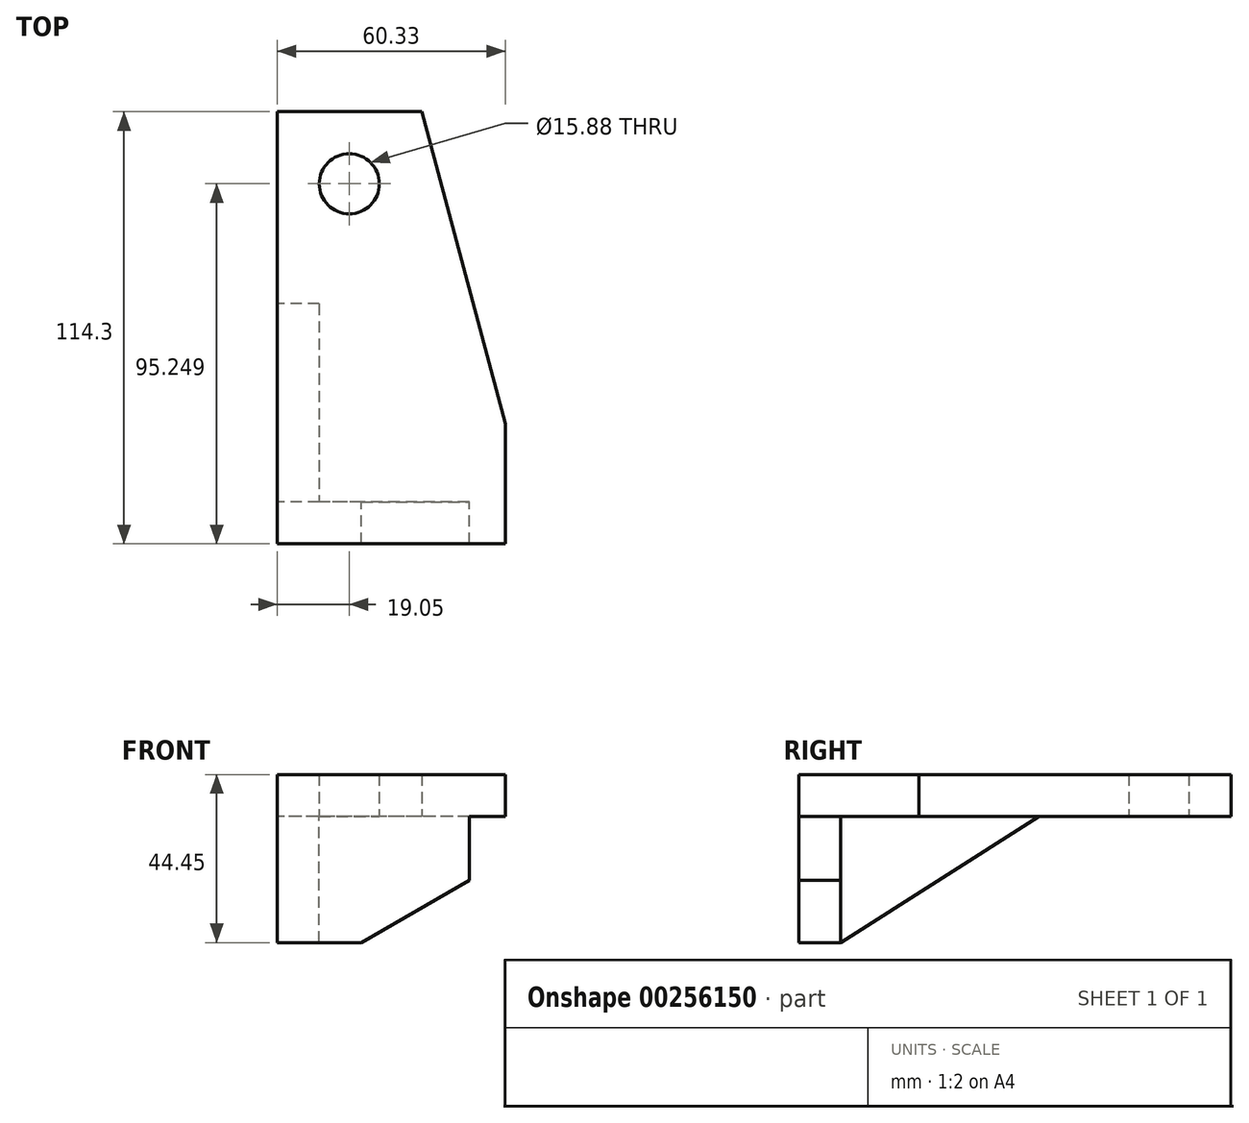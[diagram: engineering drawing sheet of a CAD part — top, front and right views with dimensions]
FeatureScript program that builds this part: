
annotation { "Feature Type Name" : "Feature", "Feature Type Description" : "" }
export const myFeature = defineFeature(function(context is Context, id is Id, definition is map)
    precondition{}
    {
        {
            var Q0;
            Q0=qCreatedBy(makeId("Right.planeOp"),FACE);
            var sketch = newSketch(context, id + "F0", { "sketchPlane" : qUnion([Q0])});
            skLineSegment(sketch, "E0", {"start": v(-71.57, 25.23) * mm, "end": v(-71.57, -19.22) * mm});
            skLineSegment(sketch, "E1", {"start": v(-71.57, 25.23) * mm, "end": v(42.73, 25.23) * mm});
            skLineSegment(sketch, "E2", {"start": v(42.73, 25.23) * mm, "end": v(42.73, 14.12) * mm});
            skLineSegment(sketch, "E3", {"start": v(-71.57, -19.22) * mm, "end": v(-60.46, -19.22) * mm});
            skLineSegment(sketch, "E4", {"start": v(42.73, 14.12) * mm, "end": v(-8.07, 14.12) * mm});
            skLineSegment(sketch, "E5", {"start": v(-8.07, 14.12) * mm, "end": v(-60.46, -19.22) * mm});
            skLineSegment(sketch, "E6", {"start": v(-60.46, -19.22) * mm, "end": v(-60.46, 25.23) * mm});
            skLineSegment(sketch, "E7", {"start": v(-8.07, 14.12) * mm, "end": v(-60.46, 14.12) * mm});
            skLineSegment(sketch, "E8", {"start": v(-60.46, 14.12) * mm, "end": v(-71.57, 14.12) * mm});
            skPoint(sketch, "E8.endSnap0", {"position": v(-71.57, 3) * mm});
            skSolve(sketch);
        }
        {
            var Q0;
            {var subQ0=sQuery(id+"F0.wireOp",EDGE,"E5");Q0=makeQuery(id+"F0.imprint","IMPRINT",FACE,{"disambiguationData":[TD([[makeQuery(id+"F0.imprint","IMPRINT",EDGE,{"derivedFrom":subQ0}),-1.0]])]});}
            extrude(context, id + "F1", {"entities" : qUnion([Q0]), "depth" : 11.1 * mm});
        }
        {
            var Q0;
            {var subQ4=sQuery(id+"F0.wireOp",EDGE,"E2");Q0=makeQuery(id+"F0.imprint","IMPRINT",FACE,{"disambiguationData":[TD([[makeQuery(id+"F0.imprint","IMPRINT",EDGE,{"derivedFrom":subQ4}),-1.0]])]});}
            var Q1;
            {var subQ3=sQuery(id+"F0.wireOp",EDGE,"E8");Q1=makeQuery(id+"F0.imprint","IMPRINT",FACE,{"disambiguationData":[TD([[makeQuery(id+"F0.imprint","IMPRINT",EDGE,{"derivedFrom":subQ3}),-1.0]])]});}
            extrude(context, id + "F2", {"entities" : qUnion([Q0, Q1]), "operationType" : NewBodyOperationType.ADD, "depth" : 60.32 * mm});
        }
        {
            var Q0;
            {var subQ0=sQuery(id+"F0.wireOp",EDGE,"E3");Q0=makeQuery(id+"F0.imprint","IMPRINT",FACE,{"disambiguationData":[TD([[makeQuery(id+"F0.imprint","IMPRINT",EDGE,{"derivedFrom":subQ0}),1.0]])]});}
            extrude(context, id + "F3", {"entities" : qUnion([Q0]), "operationType" : NewBodyOperationType.ADD, "depth" : 50.8 * mm});
        }
        {
            var Q0;
            Q0=makeQuery(id+"F2.opExtrude","SWEPT_FACE",FACE,{"disambiguationData":[OSD([sQuery(id+"F0.wireOp",EDGE,"E4"),sQuery(id+"F0.wireOp",EDGE,"E7"),sQuery(id+"F0.wireOp",EDGE,"E8")])]});
            var sketch = newSketch(context, id + "F4", { "sketchPlane" : qUnion([Q0])});
            skLineSegment(sketch, "E9", {"start": v(60.33, 39.82) * mm, "end": v(38.2, -42.73) * mm});
            skCircle(sketch, "E10", {"center": v(19.05, -23.68) * mm, "radius": 7.94 * mm});
            skSolve(sketch);
        }
        {
            var Q0;
            {var subQ0=sQuery(id+"F4.wireOp",EDGE,"E9");Q0=makeQuery(id+"F4.imprint","IMPRINT",FACE,{"disambiguationData":[TD([[makeQuery(id+"F4.imprint","IMPRINT",EDGE,{"derivedFrom":subQ0}),1.0]])]});}
            extrude(context, id + "F5", {"entities" : qUnion([Q0]), "operationType" : NewBodyOperationType.REMOVE, "oppositeDirection" : true, "depth" : 25.4 * mm});
        }
        {
            var Q0;
            Q0=makeQuery(id+"F3.opExtrude","SWEPT_FACE",FACE,{"disambiguationData":[OSD([sQuery(id+"F0.wireOp",EDGE,"E6")])]});
            var sketch = newSketch(context, id + "F6", { "sketchPlane" : qUnion([Q0])});
            skLineSegment(sketch, "E11", {"start": v(-22.23, -19.22) * mm, "end": v(-50.8, -2.72) * mm});
            skSolve(sketch);
        }
        {
            var Q0;
            Q0=makeQuery(id+"F4.imprint","IMPRINT",FACE,{"disambiguationData":[TD([[makeQuery(id+"F4.imprint","IMPRINT",EDGE,{"derivedFrom":sQuery(id+"F4.wireOp",EDGE,"E10")}),1.0]])]});
            extrude(context, id + "F7", {"entities" : qUnion([Q0]), "operationType" : NewBodyOperationType.REMOVE, "oppositeDirection" : true, "depth" : 25.4 * mm});
        }
        {
            var Q0;
            {var subQ0=sQuery(id+"F6.wireOp",EDGE,"E11");Q0=makeQuery(id+"F6.imprint","IMPRINT",FACE,{"disambiguationData":[TD([[makeQuery(id+"F6.imprint","IMPRINT",EDGE,{"derivedFrom":subQ0}),1.0]])]});}
            extrude(context, id + "F8", {"entities" : qUnion([Q0]), "operationType" : NewBodyOperationType.REMOVE, "oppositeDirection" : true, "depth" : 25.4 * mm});
        }
        {
            var Q0;
            Q0=makeQuery(id+"F1.opExtrude","SWEPT_BODY",BODY,{"disambiguationData":[OSD([sQuery(id+"F0.wireOp",EDGE,"E5"),sQuery(id+"F0.wireOp",EDGE,"E6"),sQuery(id+"F0.wireOp",EDGE,"E7")])]});
            transform(context, id + "F9", {"entities" : qUnion([Q0]), "transformType" : TransformType.TRANSLATION_3D, "dx" : 0 * mm, "dy" : 0 * mm, "dz" : 0 * mm, "makeCopy" : true});
        }
        {
            var Q0;
            Q0=makeQuery(id+"F9.opPattern","COPY",BODY,{"derivedFrom":makeQuery(id+"F1.opExtrude","SWEPT_BODY",BODY,{"disambiguationData":[OSD([sQuery(id+"F0.wireOp",EDGE,"E5"),sQuery(id+"F0.wireOp",EDGE,"E6"),sQuery(id+"F0.wireOp",EDGE,"E7")])]}),"instanceName":"1"});
            deleteBodies(context, id + "F10", {"entities" : qUnion([Q0])});
        }
    });
